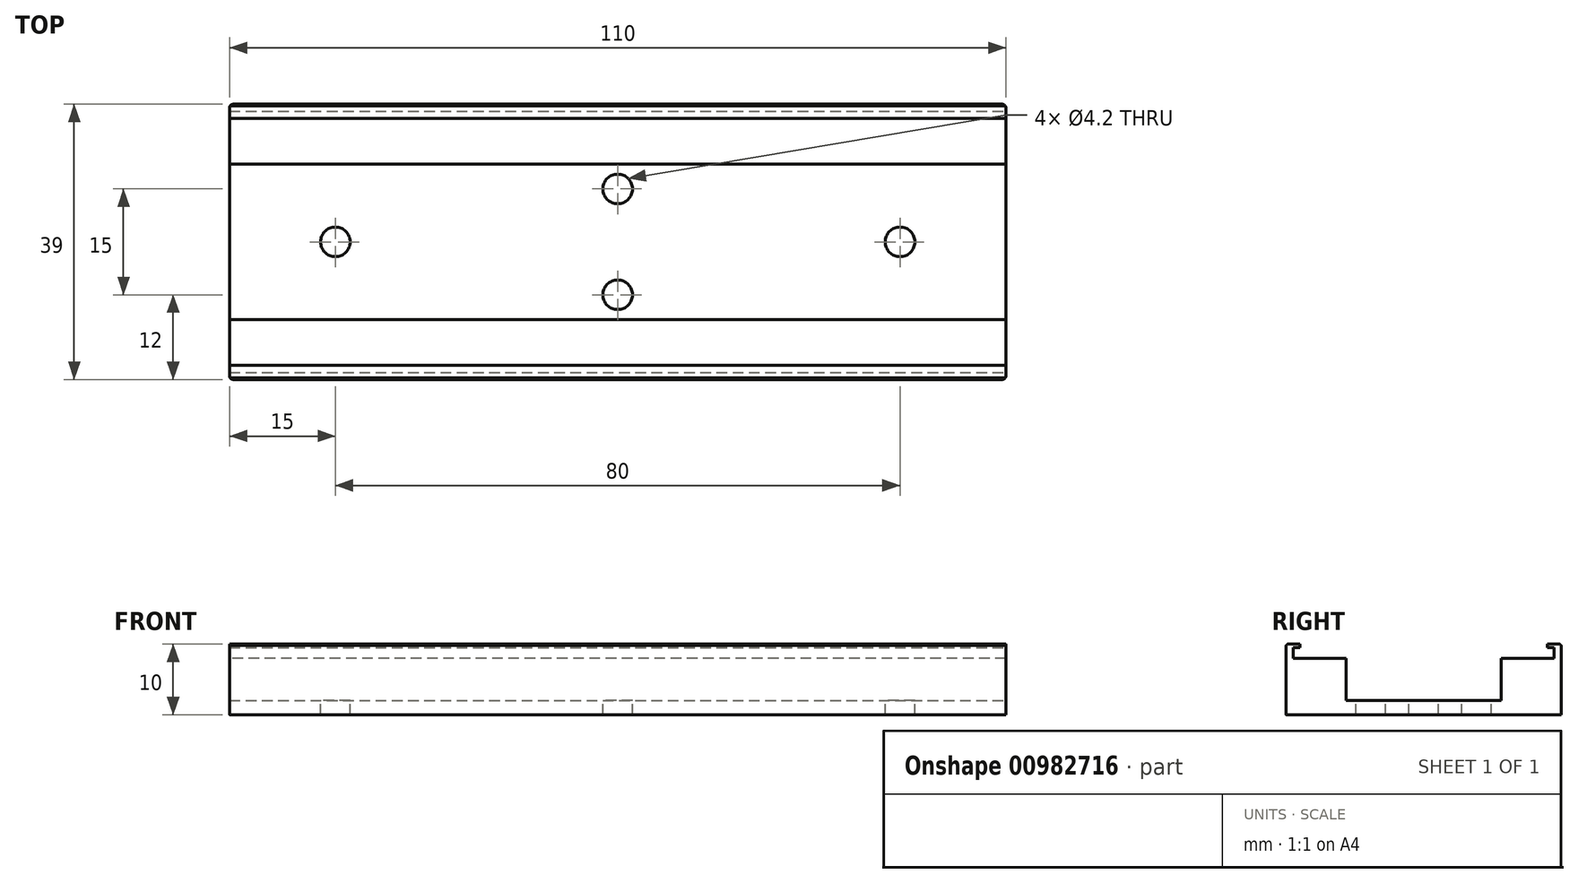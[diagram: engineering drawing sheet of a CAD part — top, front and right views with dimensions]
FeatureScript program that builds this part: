
annotation { "Feature Type Name" : "Feature", "Feature Type Description" : "" }
export const myFeature = defineFeature(function(context is Context, id is Id, definition is map)
    precondition{}
    {
        {
            var Q0;
            Q0=qCreatedBy(makeId("Right.planeOp"),FACE);
            var sketch = newSketch(context, id + "F0", { "sketchPlane" : qUnion([Q0])});
            skLineSegment(sketch, "E0.bottom", {"start": v(19.5, -5) * mm, "end": v(-19.5, -5) * mm});
            skLineSegment(sketch, "E0.top", {"start": v(19.5, 5) * mm, "end": v(-19.5, 5) * mm});
            skLineSegment(sketch, "E0.left", {"start": v(19.5, -5) * mm, "end": v(19.5, 5) * mm});
            skLineSegment(sketch, "E0.right", {"start": v(-19.5, -5) * mm, "end": v(-19.5, 5) * mm});
            skPoint(sketch, "E0.middle", {"position": v(0, 0) * mm});
            skSolve(sketch);
        }
        {
            var Q0;
            Q0=makeQuery(id+"F0.imprint","IMPRINT",FACE,{"disambiguationData":[TD([[makeQuery(id+"F0.imprint","IMPRINT",EDGE,{"derivedFrom":sQuery(id+"F0.wireOp",EDGE,"E0.bottom")}),-1.0]])]});
            extrude(context, id + "F1", {"entities" : qUnion([Q0]), "depth" : 110 * mm, "offsetDistance" : 25 * mm});
        }
        {
            var Q0;
            Q0=makeQuery(id+"F1.opExtrude","CAP_FACE",FACE,{"disambiguationData":[OSD([sQuery(id+"F0.wireOp",EDGE,"E0.bottom"),sQuery(id+"F0.wireOp",EDGE,"E0.top"),sQuery(id+"F0.wireOp",EDGE,"E0.left"),sQuery(id+"F0.wireOp",EDGE,"E0.right")])],"isStart":false});
            var sketch = newSketch(context, id + "F2", { "sketchPlane" : qUnion([Q0])});
            skLineSegment(sketch, "E1.bottom", {"start": v(17.5, 4.5) * mm, "end": v(-17.5, 4.5) * mm});
            skLineSegment(sketch, "E1.top", {"start": v(17.5, 5.5) * mm, "end": v(-17.5, 5.5) * mm});
            skLineSegment(sketch, "E1.left", {"start": v(17.5, 4.5) * mm, "end": v(17.5, 5.5) * mm});
            skLineSegment(sketch, "E1.right", {"start": v(-17.5, 4.5) * mm, "end": v(-17.5, 5.5) * mm});
            skPoint(sketch, "E1.middle", {"position": v(0, 5) * mm});
            skSolve(sketch);
        }
        {
            var Q0;
            Q0=qSketchRegion(id+"F2",true);
            extrude(context, id + "F3", {"entities" : qUnion([Q0]), "operationType" : NewBodyOperationType.REMOVE, "oppositeDirection" : true, "depth" : 110 * mm, "offsetDistance" : 25 * mm});
        }
        {
            var Q0;
            Q0=makeQuery(id+"F1.opExtrude","CAP_FACE",FACE,{"disambiguationData":[OSD([sQuery(id+"F0.wireOp",EDGE,"E0.bottom"),sQuery(id+"F0.wireOp",EDGE,"E0.top"),sQuery(id+"F0.wireOp",EDGE,"E0.left"),sQuery(id+"F0.wireOp",EDGE,"E0.right")])],"isStart":false});
            var sketch = newSketch(context, id + "F4", { "sketchPlane" : qUnion([Q0])});
            skLineSegment(sketch, "E2.bottom", {"start": v(18.5, 3) * mm, "end": v(-18.5, 3) * mm});
            skLineSegment(sketch, "E2.left", {"start": v(18.5, 3) * mm, "end": v(18.5, 4.5) * mm});
            skLineSegment(sketch, "E2.right", {"start": v(-18.5, 3) * mm, "end": v(-18.5, 4.5) * mm});
            skPoint(sketch, "E2.middle", {"position": v(0, 3.75) * mm});
            skLineSegment(sketch, "E3", {"start": v(-18.5, 4.5) * mm, "end": v(-17.5, 4.5) * mm});
            skLineSegment(sketch, "E4", {"start": v(-17.5, 4.5) * mm, "end": v(-17.5, 5.54) * mm});
            skLineSegment(sketch, "E5", {"start": v(-17.5, 5.54) * mm, "end": v(17.5, 5.54) * mm});
            skLineSegment(sketch, "E6", {"start": v(17.5, 5.54) * mm, "end": v(17.5, 4.5) * mm});
            skLineSegment(sketch, "E7", {"start": v(17.5, 4.5) * mm, "end": v(18.5, 4.5) * mm});
            skSolve(sketch);
        }
        {
            var Q0;
            Q0=qSketchRegion(id+"F4",true);
            extrude(context, id + "F5", {"entities" : qUnion([Q0]), "operationType" : NewBodyOperationType.REMOVE, "oppositeDirection" : true, "depth" : 110 * mm, "offsetDistance" : 25 * mm});
        }
        {
            var Q0;
            Q0=makeQuery(id+"F1.opExtrude","CAP_FACE",FACE,{"disambiguationData":[OSD([sQuery(id+"F0.wireOp",EDGE,"E0.bottom"),sQuery(id+"F0.wireOp",EDGE,"E0.top"),sQuery(id+"F0.wireOp",EDGE,"E0.left"),sQuery(id+"F0.wireOp",EDGE,"E0.right")])],"isStart":false});
            var sketch = newSketch(context, id + "F6", { "sketchPlane" : qUnion([Q0])});
            skLineSegment(sketch, "E8.bottom", {"start": v(11, -3) * mm, "end": v(-11, -3) * mm});
            skLineSegment(sketch, "E8.top", {"start": v(11, 9) * mm, "end": v(-11, 9) * mm});
            skLineSegment(sketch, "E8.left", {"start": v(11, -3) * mm, "end": v(11, 9) * mm});
            skLineSegment(sketch, "E8.right", {"start": v(-11, -3) * mm, "end": v(-11, 9) * mm});
            skPoint(sketch, "E8.middle", {"position": v(0, 3) * mm});
            skSolve(sketch);
        }
        {
            var Q0;
            Q0=qSketchRegion(id+"F6",true);
            extrude(context, id + "F7", {"entities" : qUnion([Q0]), "operationType" : NewBodyOperationType.REMOVE, "oppositeDirection" : true, "depth" : 110 * mm, "offsetDistance" : 25 * mm});
        }
        {
            var Q0;
            Q0=makeQuery(id+"F7.boolean.opBoolean","COPY",FACE,{"derivedFrom":makeQuery(id+"F7.opExtrude","SWEPT_FACE",FACE,{"disambiguationData":[OSD([sQuery(id+"F6.wireOp",EDGE,"E8.bottom")])]})});
            var sketch = newSketch(context, id + "F8", { "sketchPlane" : qUnion([Q0])});
            skLineSegment(sketch, "E9", {"start": v(55, 35.66) * mm, "end": v(55, -46.06) * mm, "construction": true});
            skLineSegment(sketch, "E10", {"start": v(119.12, 0) * mm, "end": v(-20.16, 0) * mm, "construction": true});
            skCircle(sketch, "E11", {"center": v(15, 0) * mm, "radius": 2.1 * mm});
            skCircle(sketch, "E12.MirrorC", {"center": v(95, 0) * mm, "radius": 2.1 * mm});
            skCircle(sketch, "E13", {"center": v(55, -7.5) * mm, "radius": 2.1 * mm});
            skCircle(sketch, "E14.MirrorC", {"center": v(55, 7.5) * mm, "radius": 2.1 * mm});
            skSolve(sketch);
        }
        {
            var Q0;
            Q0=qSketchRegion(id+"F8",true);
            extrude(context, id + "F9", {"entities" : qUnion([Q0]), "operationType" : NewBodyOperationType.REMOVE, "oppositeDirection" : true, "depth" : 25 * mm, "offsetDistance" : 25 * mm});
        }
        {
            var Q0;
            Q0=makeQuery(id+"F1.opExtrude","SWEPT_EDGE",EDGE,{"disambiguationData":[OSD([sQuery(id+"F0.wireOp",EDGE,"E0.top"),sQuery(id+"F0.wireOp",EDGE,"E0.right")])]});
            var Q1;
            Q1=makeQuery(id+"F1.opExtrude","SWEPT_EDGE",EDGE,{"disambiguationData":[OSD([sQuery(id+"F0.wireOp",EDGE,"E0.top"),sQuery(id+"F0.wireOp",EDGE,"E0.left")])]});
            chamfer(context, id + "F10", {"entities" : qUnion([Q0, Q1]), "width" : 0.2 * mm, "tangentPropagation" : true});
        }
        {
            var Q0;
            Q0=makeQuery(id+"F1.opExtrude","CAP_EDGE",EDGE,{"disambiguationData":[OSD([sQuery(id+"F0.wireOp",EDGE,"E0.right")])],"isStart":true});
            var Q1;
            Q1=makeQuery(id+"F1.opExtrude","CAP_EDGE",EDGE,{"disambiguationData":[OSD([sQuery(id+"F0.wireOp",EDGE,"E0.left")])],"isStart":true});
            var Q2;
            Q2=makeQuery(id+"F1.opExtrude","CAP_EDGE",EDGE,{"disambiguationData":[OSD([sQuery(id+"F0.wireOp",EDGE,"E0.right")])],"isStart":false});
            var Q3;
            Q3=makeQuery(id+"F1.opExtrude","CAP_EDGE",EDGE,{"disambiguationData":[OSD([sQuery(id+"F0.wireOp",EDGE,"E0.left")])],"isStart":false});
            fillet(context, id + "F11", {"entities" : qUnion([Q0, Q1, Q2, Q3]), "radius" : 0.5 * mm, "tangentPropagation" : true, "allowEdgeOverflow" : false});
        }
    });
